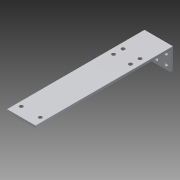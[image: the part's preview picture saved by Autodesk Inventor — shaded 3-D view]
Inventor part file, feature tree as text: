
AUTODESK INVENTOR PART (.ipt)
format: ipt  version: 2014 (Build 180170000, 170)  size: 119,808 bytes
history: native  units: in
note: dims shown in document units (in); Inventor stores cm internally (conversion verified against a paired STEP export)
features: sketch x2, sheet_metal_op x1, extrude x1, other x1
ambient origin geometry x8: Origin, YZ Plane, XZ Plane, XY Plane, X Axis, Y Axis, Z Axis, Center Point
bodies: Solid1 (feature_tree)
feature tree (5):
  sheet_metal_op  "Face1"
  extrude  "Extrusion1"  Depth=1.0in
  sketch  "Sketch1"  dims[d0=1.5in d1=1.0in]
  other  "Plate1"
  sketch  "Sketch2"  dims[d2=0.164in d3=0.5in d4=0.25in d13=0.125in d14=0.192in d15=7.25in d16=0.5in d17=0.5in d18=0.125in d19=0.0in d21=0.5in d22=0.4485in d23=4.817in d24=0.7874in d26=1.0in d27=0.3937in d29=1.0in]
